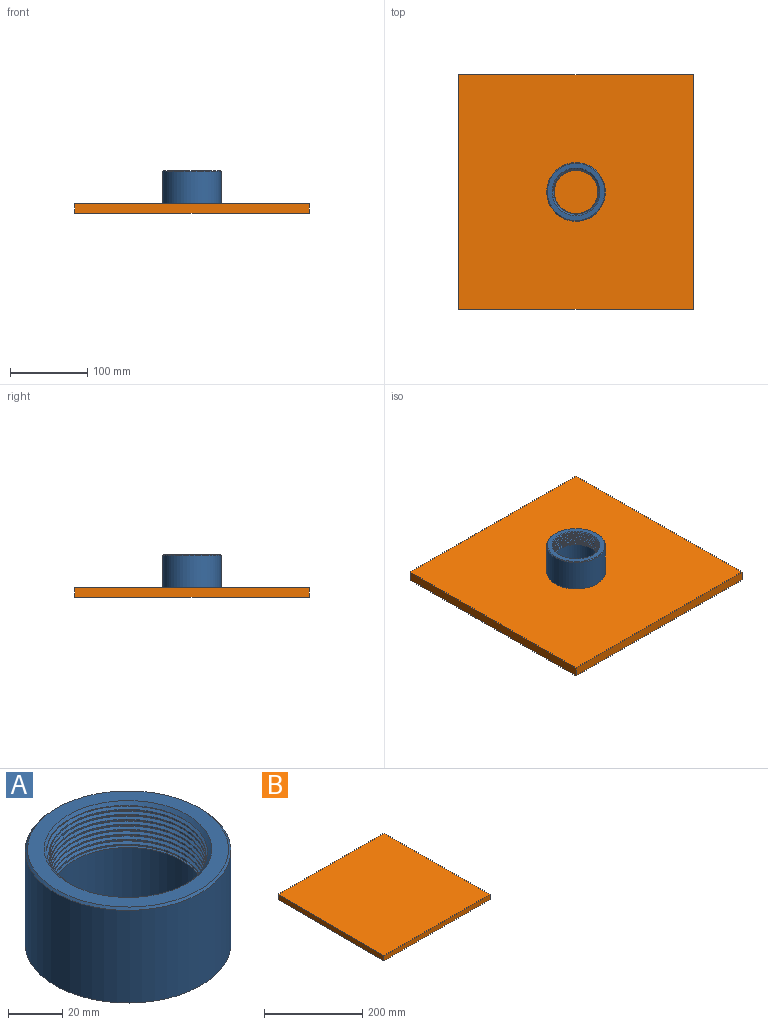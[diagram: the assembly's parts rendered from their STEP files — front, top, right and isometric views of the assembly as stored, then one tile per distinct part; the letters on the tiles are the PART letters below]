
ASSEMBLY  parts=2 mates=1
PART A: 11 faces, bbox 76.7x76.7x46.2 mm
  f0: cylinder r=28.13mm len=56.26mm, axis (0,0,1), area 4179.5mm2, adj f1,f10
  f1: plane 76.2x76.2mm, normal (0,0,-1), area 2074.5mm2, adj f0,f2
  f2: cylinder r=38.1mm len=76.2mm, axis (0,0,-1), area 10049.3mm2, adj f1,f3
  f3: cone r=37.22mm half-angle=45deg, axis (0,0,-1), area 295.6mm2, adj f2,f4
  f4: plane 74.43x74.43mm, normal (0,0,1), area 1323.3mm2, adj f3,f5
  f5: cone r=31.05mm half-angle=45deg, axis (0,0,1), area 423mm2, adj f4,f6,f7,f8,f9
  f6: bspline ~58.56x58.46mm, area 832.3mm2, adj f5,f7,f9,f10
  f7: bspline ~60.93x60.83mm, area 1095.1mm2, adj f5,f6,f8,f10
  f8: cone r=30.16mm half-angle=1.8deg, axis (0,0,1), area 478.1mm2, adj f5,f7,f9,f10
  f9: bspline ~60.18x53.1mm, area 9263.5mm2, adj f5,f6,f8,f10
  f10: plane 58.58x58.38mm, normal (0,0,1), area 143.1mm2, adj f0,f6,f7,f8,f9
PART B: 6 faces, bbox 304.8x304.8x12.7 mm
  f0: plane 304.8x12.7mm, normal (0,1,0), area 3871mm2, adj f1,f3,f4,f5
  f1: plane 304.8x12.7mm, normal (-1,0,0), area 3871mm2, adj f0,f2,f4,f5
  f2: plane 304.8x12.7mm, normal (0,-1,0), area 3871mm2, adj f1,f3,f4,f5
  f3: plane 304.8x12.7mm, normal (1,0,0), area 3871mm2, adj f0,f2,f4,f5
  f4: plane 304.8x304.8mm, normal (0,0,1), area 92903mm2, adj f0,f1,f2,f3
  f5: plane 304.8x304.8mm, normal (0,0,-1), area 92903mm2, adj f0,f1,f2,f3
PLACE A rot(axis=(0,0,1),0deg) t=(27.82,-17.43,-22.45)mm
PLACE B t=(-56.36,74.23,-56.58)mm
MATE planar A.f0 <-> B.f4  axis (0,0,-1) through (27.82,-17.43,-43.88)mm
